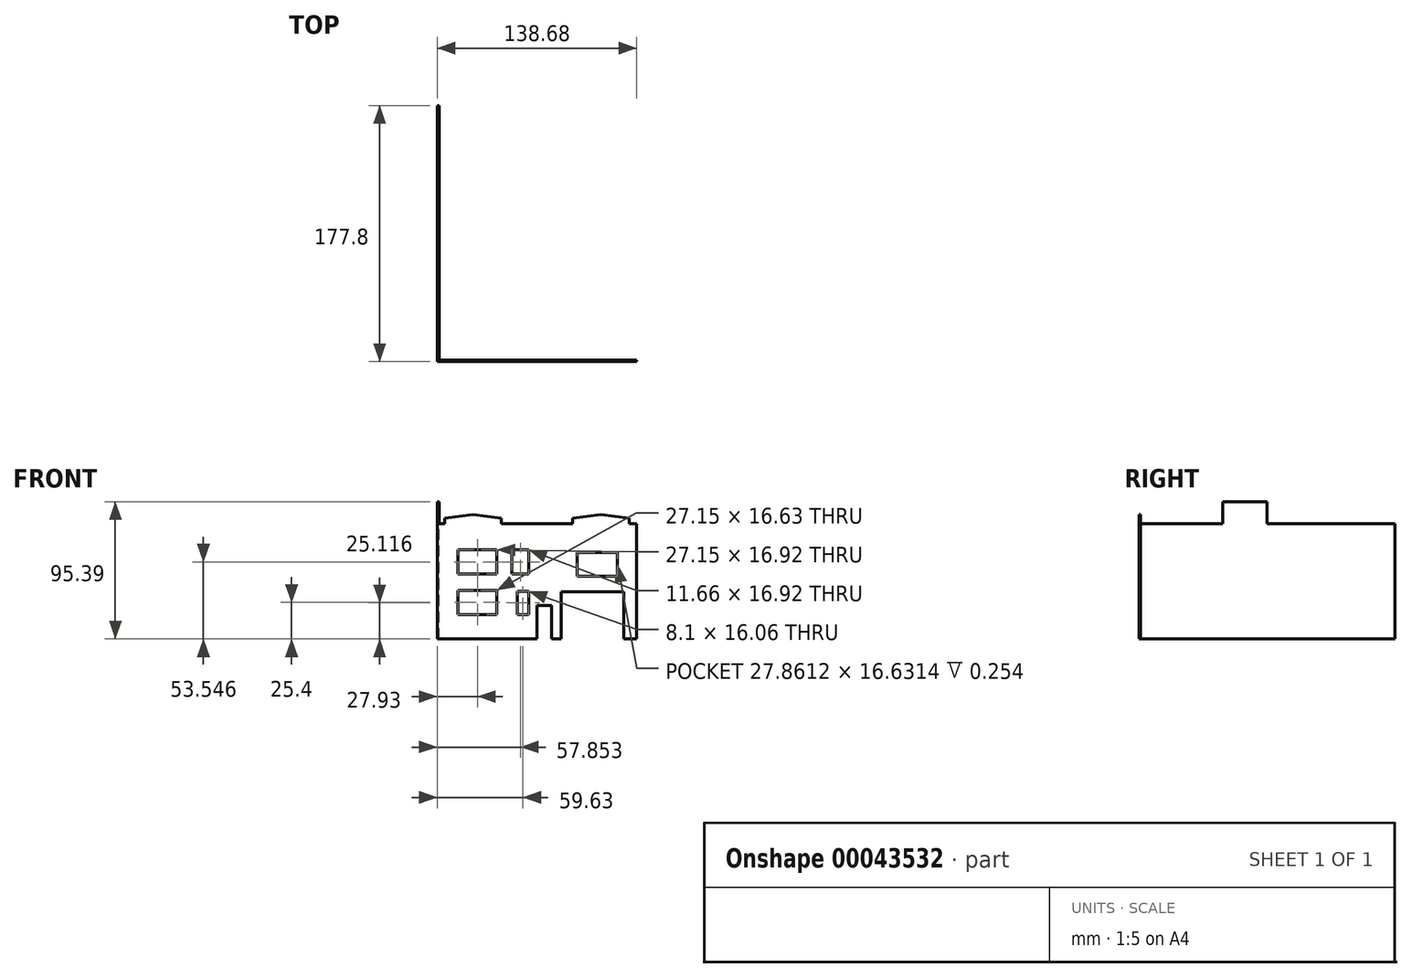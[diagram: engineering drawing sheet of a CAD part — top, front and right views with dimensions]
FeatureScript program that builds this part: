
annotation { "Feature Type Name" : "Feature", "Feature Type Description" : "" }
export const myFeature = defineFeature(function(context is Context, id is Id, definition is map)
    precondition{}
    {
        {
            var Q0;
            Q0=qCreatedBy(makeId("Front.planeOp"),FACE);
            var sketch = newSketch(context, id + "F0", { "sketchPlane" : qUnion([Q0])});
            skLineSegment(sketch, "E0", {"start": v(0, 0) * mm, "end": v(0, 8026.4) * mm});
            skLineSegment(sketch, "E1", {"start": v(0, 8026.4) * mm, "end": v(508, 8026.4) * mm});
            skLineSegment(sketch, "E2", {"start": v(508, 8026.4) * mm, "end": v(508, 8382) * mm});
            skLineSegment(sketch, "E3", {"start": v(508, 8382) * mm, "end": v(2489.2, 8636) * mm});
            skLineSegment(sketch, "E4", {"start": v(2489.2, 8636) * mm, "end": v(2489.2, 0) * mm, "construction": true});
            skLineSegment(sketch, "E5.MirrorCS", {"start": v(4470.4, 8382) * mm, "end": v(2489.2, 8636) * mm});
            skLineSegment(sketch, "E6.MirrorCS", {"start": v(4470.4, 8026.4) * mm, "end": v(4470.4, 8382) * mm});
            skLineSegment(sketch, "E7", {"start": v(4470.4, 8026.4) * mm, "end": v(9398, 8026.4) * mm});
            skLineSegment(sketch, "E8", {"start": v(6934.2, 8026.4) * mm, "end": v(6934.2, 0) * mm, "construction": true});
            skLineSegment(sketch, "E9.MirrorCS", {"start": v(9398, 8026.4) * mm, "end": v(9398, 8382) * mm});
            skLineSegment(sketch, "E10.MirrorCS", {"start": v(9398, 8382) * mm, "end": v(11379.2, 8636) * mm});
            skLineSegment(sketch, "E11.MirrorCS", {"start": v(13360.4, 8382) * mm, "end": v(11379.2, 8636) * mm});
            skLineSegment(sketch, "E12.MirrorCS", {"start": v(13868.4, 8026.4) * mm, "end": v(13360.4, 8026.4) * mm});
            skLineSegment(sketch, "E13.MirrorCS", {"start": v(13360.4, 8026.4) * mm, "end": v(13360.4, 8382) * mm});
            skLineSegment(sketch, "E14", {"start": v(13868.4, 8026.4) * mm, "end": v(13868.4, 0) * mm});
            skLineSegment(sketch, "E15", {"start": v(13868.4, 0) * mm, "end": v(0, 0) * mm});
            skLineSegment(sketch, "E16.bottom", {"start": v(9737.03, 4366.63) * mm, "end": v(12523.15, 4366.63) * mm});
            skLineSegment(sketch, "E16.top", {"start": v(9737.03, 6029.77) * mm, "end": v(12523.15, 6029.77) * mm});
            skLineSegment(sketch, "E16.left", {"start": v(9737.03, 4366.63) * mm, "end": v(9737.03, 6029.77) * mm});
            skLineSegment(sketch, "E16.right", {"start": v(12523.15, 4366.63) * mm, "end": v(12523.15, 6029.77) * mm});
            skLineSegment(sketch, "E17", {"start": v(8614.05, 0) * mm, "end": v(8614.05, 3286.3) * mm});
            skLineSegment(sketch, "E18", {"start": v(8614.05, 3286.3) * mm, "end": v(12963.81, 3286.3) * mm});
            skLineSegment(sketch, "E19", {"start": v(12963.81, 3286.3) * mm, "end": v(12963.81, 0) * mm});
            skLineSegment(sketch, "E20", {"start": v(7960.16, 0) * mm, "end": v(7960.16, 2333.9) * mm});
            skLineSegment(sketch, "E21", {"start": v(7960.16, 2333.9) * mm, "end": v(6934.2, 2333.9) * mm});
            skLineSegment(sketch, "E22", {"start": v(6934.2, 2333.9) * mm, "end": v(6934.2, 0) * mm});
            skLineSegment(sketch, "E23.bottom", {"start": v(1435.52, 3371.58) * mm, "end": v(4150.57, 3371.58) * mm});
            skLineSegment(sketch, "E23.top", {"start": v(1435.52, 1708.44) * mm, "end": v(4150.57, 1708.44) * mm});
            skLineSegment(sketch, "E23.left", {"start": v(1435.52, 3371.58) * mm, "end": v(1435.52, 1708.44) * mm});
            skLineSegment(sketch, "E23.right", {"start": v(4150.57, 3371.58) * mm, "end": v(4150.57, 1708.44) * mm});
            skLineSegment(sketch, "E24.bottom", {"start": v(4150.57, 4508.78) * mm, "end": v(1435.52, 4508.78) * mm});
            skLineSegment(sketch, "E24.top", {"start": v(4150.57, 6200.35) * mm, "end": v(1435.52, 6200.35) * mm});
            skLineSegment(sketch, "E24.left", {"start": v(4150.57, 4508.78) * mm, "end": v(4150.57, 6200.35) * mm});
            skLineSegment(sketch, "E24.right", {"start": v(1435.52, 4508.78) * mm, "end": v(1435.52, 6200.35) * mm});
            skLineSegment(sketch, "E25.bottom", {"start": v(5557.84, 1708.44) * mm, "end": v(6368.1, 1708.44) * mm});
            skLineSegment(sketch, "E25.top", {"start": v(5557.84, 3314.72) * mm, "end": v(6368.1, 3314.72) * mm});
            skLineSegment(sketch, "E25.left", {"start": v(5557.84, 1708.44) * mm, "end": v(5557.84, 3314.72) * mm});
            skLineSegment(sketch, "E25.right", {"start": v(6368.1, 1708.44) * mm, "end": v(6368.1, 3314.72) * mm});
            skLineSegment(sketch, "E26.bottom", {"start": v(5202.47, 4508.78) * mm, "end": v(6368.1, 4508.78) * mm});
            skLineSegment(sketch, "E26.top", {"start": v(5202.47, 6200.35) * mm, "end": v(6368.1, 6200.35) * mm});
            skLineSegment(sketch, "E26.left", {"start": v(5202.47, 4508.78) * mm, "end": v(5202.47, 6200.35) * mm});
            skLineSegment(sketch, "E26.right", {"start": v(6368.1, 4508.78) * mm, "end": v(6368.1, 6200.35) * mm});
            skSolve(sketch);
        }
        {
            var Q0;
            {var subQ3=sQuery(id+"F0.wireOp",EDGE,"E0");Q0=makeQuery(id+"F0.imprint","IMPRINT",FACE,{"disambiguationData":[TD([[makeQuery(id+"F0.imprint","IMPRINT",EDGE,{"derivedFrom":subQ3}),-1.0]])]});}
            var Q1;
            Q1=makeQuery(id+"F0.imprint","IMPRINT",FACE,{"disambiguationData":[TD([[makeQuery(id+"F0.imprint","IMPRINT",EDGE,{"derivedFrom":sQuery(id+"F0.wireOp",EDGE,"E16.bottom")}),1.0]])]});
            extrude(context, id + "F1", {"entities" : qUnion([Q0, Q1]), "oppositeDirection" : true, "depth" : 101.6 * mm});
        }
        {
            var Q0;
            Q0=makeQuery(id+"F0.imprint","IMPRINT",FACE,{"disambiguationData":[TD([[makeQuery(id+"F0.imprint","IMPRINT",EDGE,{"derivedFrom":sQuery(id+"F0.wireOp",EDGE,"E16.bottom")}),1.0]])]});
            extrude(context, id + "F2", {"entities" : qUnion([Q0]), "operationType" : NewBodyOperationType.REMOVE, "oppositeDirection" : true, "depth" : 25.4 * mm});
        }
        {
            var Q0;
            Q0=qCreatedBy(makeId("Right.planeOp"),FACE);
            var sketch = newSketch(context, id + "F3", { "sketchPlane" : qUnion([Q0])});
            skLineSegment(sketch, "E27", {"start": v(0, 0) * mm, "end": v(0, 8026.4) * mm});
            skLineSegment(sketch, "E28", {"start": v(0, 8026.4) * mm, "end": v(5817.12, 8026.4) * mm});
            skLineSegment(sketch, "E29", {"start": v(0, 0) * mm, "end": v(17780, 0) * mm});
            skLineSegment(sketch, "E30", {"start": v(17780, 0) * mm, "end": v(17780, 8026.4) * mm});
            skPoint(sketch, "E31.orphan", {"position": v(5817.12, 8026.4) * mm});
            skLineSegment(sketch, "E32", {"start": v(5817.12, 8026.4) * mm, "end": v(5817.12, 9539.34) * mm});
            skLineSegment(sketch, "E33", {"start": v(5817.12, 9539.34) * mm, "end": v(8907.93, 9539.34) * mm});
            skLineSegment(sketch, "E34", {"start": v(8907.93, 9539.34) * mm, "end": v(8907.93, 8026.4) * mm});
            skLineSegment(sketch, "E35.trimOffspring", {"start": v(8907.93, 8026.4) * mm, "end": v(17780, 8026.4) * mm});
            skSolve(sketch);
        }
        {
            var Q0;
            Q0=makeQuery(id+"F3.imprint","IMPRINT",FACE,{"disambiguationData":[TD([[makeQuery(id+"F3.imprint","IMPRINT",EDGE,{"derivedFrom":sQuery(id+"F3.wireOp",EDGE,"E27")}),-1.0]])]});
            extrude(context, id + "F4", {"entities" : qUnion([Q0]), "operationType" : NewBodyOperationType.ADD, "depth" : 152.4 * mm});
        }
        {
            var Q0;
            Q0=makeQuery(id+"F1.opExtrude","SWEPT_BODY",BODY,{"disambiguationData":[OSD([sQuery(id+"F0.wireOp",EDGE,"E0"),sQuery(id+"F0.wireOp",EDGE,"E1"),sQuery(id+"F0.wireOp",EDGE,"E2"),sQuery(id+"F0.wireOp",EDGE,"E3"),sQuery(id+"F0.wireOp",EDGE,"E5.MirrorCS"),sQuery(id+"F0.wireOp",EDGE,"E6.MirrorCS"),sQuery(id+"F0.wireOp",EDGE,"E7"),sQuery(id+"F0.wireOp",EDGE,"E9.MirrorCS"),sQuery(id+"F0.wireOp",EDGE,"E10.MirrorCS"),sQuery(id+"F0.wireOp",EDGE,"E11.MirrorCS"),sQuery(id+"F0.wireOp",EDGE,"E12.MirrorCS"),sQuery(id+"F0.wireOp",EDGE,"E13.MirrorCS"),sQuery(id+"F0.wireOp",EDGE,"E14"),sQuery(id+"F0.wireOp",EDGE,"E15"),sQuery(id+"F0.wireOp",EDGE,"E17"),sQuery(id+"F0.wireOp",EDGE,"E18"),sQuery(id+"F0.wireOp",EDGE,"E19"),sQuery(id+"F0.wireOp",EDGE,"E20"),sQuery(id+"F0.wireOp",EDGE,"E21"),sQuery(id+"F0.wireOp",EDGE,"E22"),sQuery(id+"F0.wireOp",EDGE,"E23.bottom"),sQuery(id+"F0.wireOp",EDGE,"E23.top"),sQuery(id+"F0.wireOp",EDGE,"E23.left"),sQuery(id+"F0.wireOp",EDGE,"E23.right"),sQuery(id+"F0.wireOp",EDGE,"E24.bottom"),sQuery(id+"F0.wireOp",EDGE,"E24.top"),sQuery(id+"F0.wireOp",EDGE,"E24.left"),sQuery(id+"F0.wireOp",EDGE,"E24.right"),sQuery(id+"F0.wireOp",EDGE,"E25.bottom"),sQuery(id+"F0.wireOp",EDGE,"E25.top"),sQuery(id+"F0.wireOp",EDGE,"E25.left"),sQuery(id+"F0.wireOp",EDGE,"E25.right"),sQuery(id+"F0.wireOp",EDGE,"E26.bottom"),sQuery(id+"F0.wireOp",EDGE,"E26.top"),sQuery(id+"F0.wireOp",EDGE,"E26.left"),sQuery(id+"F0.wireOp",EDGE,"E26.right")])]});
            var Q1;
            Q1=qCreatedBy(makeId("Origin.pointOp"),VERTEX);
            transform(context, id + "F5", {"entities" : qUnion([Q0]), "transformType" : TransformType.SCALE_UNIFORMLY, "scale" : 1 / 100, "makeCopy" : false, "scalePoint" : qUnion([Q1])});
        }
    });
